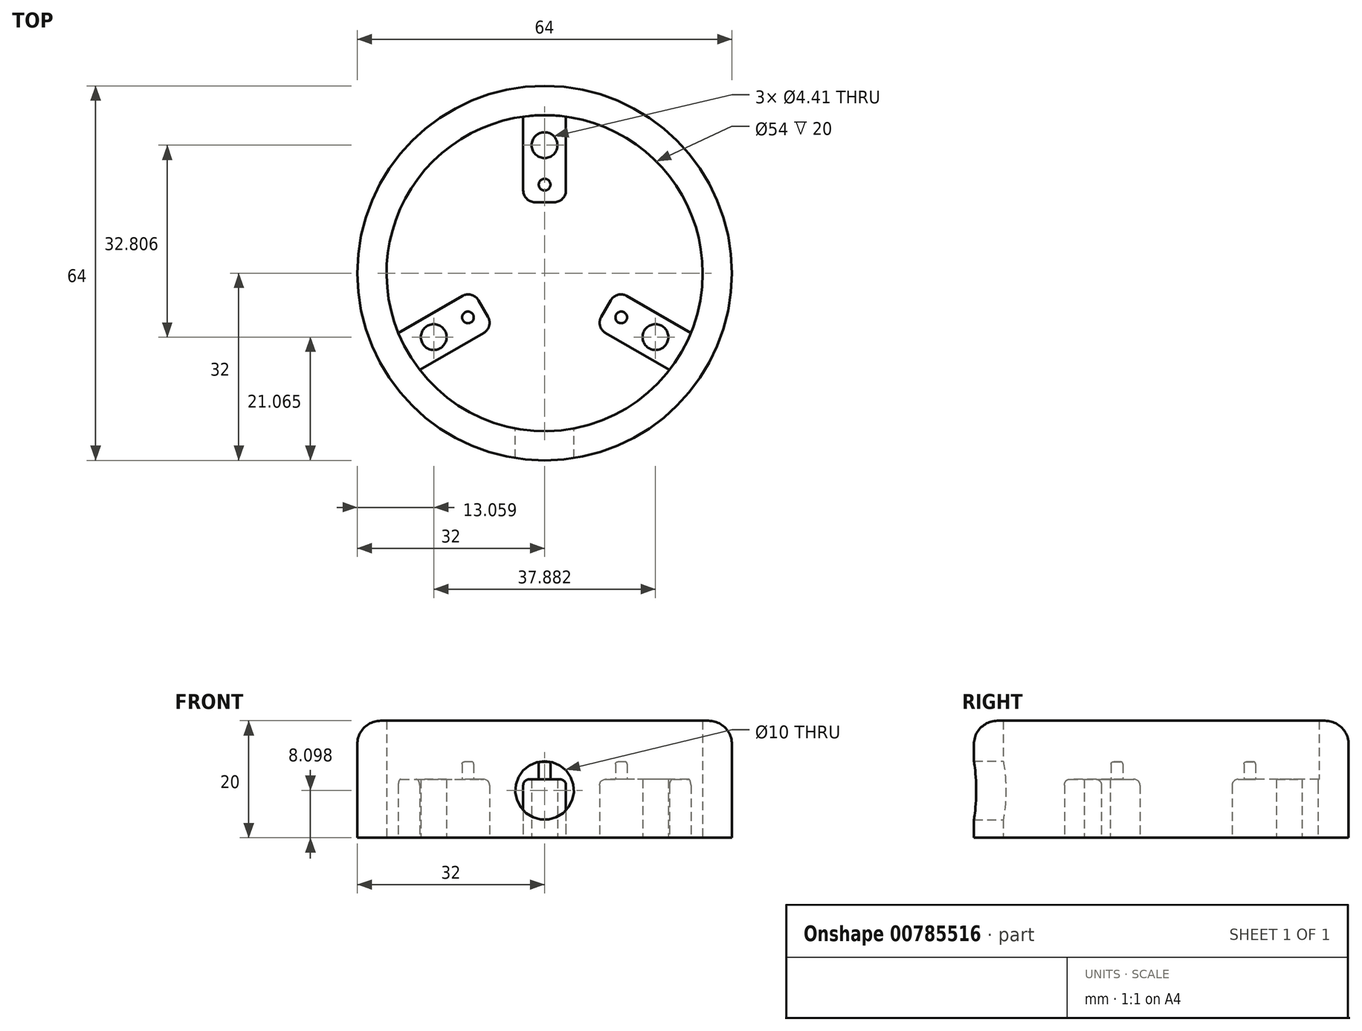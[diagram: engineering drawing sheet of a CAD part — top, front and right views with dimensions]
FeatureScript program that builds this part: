
annotation { "Feature Type Name" : "Feature", "Feature Type Description" : "" }
export const myFeature = defineFeature(function(context is Context, id is Id, definition is map)
    precondition{}
    {
        {
            var Q0;
            Q0=qCreatedBy(makeId("Top.planeOp"),FACE);
            var sketch = newSketch(context, id + "F0", { "sketchPlane" : qUnion([Q0])});
            skCircle(sketch, "E0", {"center": v(0, 0) * mm, "radius": 27 * mm});
            skCircle(sketch, "E1", {"center": v(0, 15.13) * mm, "radius": 1 * mm});
            skCircle(sketch, "E2.1.0", {"center": v(-13.1, -7.56) * mm, "radius": 1 * mm});
            skCircle(sketch, "E2.2.0", {"center": v(13.1, -7.56) * mm, "radius": 1 * mm});
            skLineSegment(sketch, "E3.right", {"start": v(3.65, 26.75) * mm, "end": v(3.65, 14.13) * mm});
            skLineSegment(sketch, "E4.1.0", {"start": v(-21.34, -16.54) * mm, "end": v(-10.4, -10.23) * mm});
            skLineSegment(sketch, "E4.1.1", {"start": v(-25, -10.21) * mm, "end": v(-14.06, -3.9) * mm});
            skLineSegment(sketch, "E4.2.0", {"start": v(25, -10.21) * mm, "end": v(14.06, -3.9) * mm});
            skLineSegment(sketch, "E4.2.1", {"start": v(21.34, -16.54) * mm, "end": v(10.4, -10.23) * mm});
            skPoint(sketch, "E5.orphan", {"position": v(-3.65, 29.24) * mm});
            skPoint(sketch, "E6.orphan", {"position": v(3.65, 29.24) * mm});
            skPoint(sketch, "E7.orphan", {"position": v(27.15, -11.46) * mm});
            skPoint(sketch, "E8.orphan", {"position": v(23.5, -17.78) * mm});
            skPoint(sketch, "E9.orphan", {"position": v(-27.15, -11.46) * mm});
            skPoint(sketch, "E10.orphan", {"position": v(-23.5, -17.78) * mm});
            skLineSegment(sketch, "E11", {"start": v(-1.65, 12.13) * mm, "end": v(1.65, 12.13) * mm});
            skLineSegment(sketch, "E12", {"start": v(-9.68, -7.5) * mm, "end": v(-11.33, -4.63) * mm});
            skLineSegment(sketch, "E13", {"start": v(9.68, -7.5) * mm, "end": v(11.33, -4.63) * mm});
            skPoint(sketch, "E14.trimOffspring.end.orphan", {"position": v(3.65, 1.01) * mm});
            skPoint(sketch, "E15.trimOffspring.end.orphan", {"position": v(-3.65, 1.01) * mm});
            skLineSegment(sketch, "E16", {"start": v(-3.65, 14.13) * mm, "end": v(-3.65, 26.75) * mm});
            skCircle(sketch, "E17.0", {"center": v(0, 0) * mm, "radius": 32 * mm});
            skCircle(sketch, "E18", {"center": v(0, 21.87) * mm, "radius": 2.2 * mm});
            skCircle(sketch, "E19.1.0", {"center": v(-18.94, -10.94) * mm, "radius": 2.2 * mm});
            skCircle(sketch, "E19.2.0", {"center": v(18.94, -10.94) * mm, "radius": 2.2 * mm});
            skPoint(sketch, "E20.visualSharp", {"position": v(-3.65, 12.13) * mm});
            skArc(sketch, "E20.filletArc", {"start": v(-3.65, 14.13) * mm, "mid": v(-3.07, 12.71) * mm, "end": v(-1.65, 12.13) * mm});
            skPoint(sketch, "E21.visualSharp", {"position": v(3.65, 12.13) * mm});
            skArc(sketch, "E21.filletArc", {"start": v(1.65, 12.13) * mm, "mid": v(3.07, 12.71) * mm, "end": v(3.65, 14.13) * mm});
            skPoint(sketch, "E22.visualSharp", {"position": v(12.33, -2.9) * mm});
            skArc(sketch, "E22.filletArc", {"start": v(14.06, -3.9) * mm, "mid": v(12.54, -3.7) * mm, "end": v(11.33, -4.63) * mm});
            skPoint(sketch, "E23.visualSharp", {"position": v(8.68, -9.23) * mm});
            skArc(sketch, "E23.filletArc", {"start": v(9.68, -7.5) * mm, "mid": v(9.48, -9.01) * mm, "end": v(10.4, -10.23) * mm});
            skPoint(sketch, "E24.visualSharp", {"position": v(-8.68, -9.23) * mm});
            skArc(sketch, "E24.filletArc", {"start": v(-10.4, -10.23) * mm, "mid": v(-9.48, -9.01) * mm, "end": v(-9.68, -7.5) * mm});
            skPoint(sketch, "E25.visualSharp", {"position": v(-12.33, -2.9) * mm});
            skArc(sketch, "E25.filletArc", {"start": v(-11.33, -4.63) * mm, "mid": v(-12.54, -3.7) * mm, "end": v(-14.06, -3.9) * mm});
            skSolve(sketch);
        }
        {
            var Q0;
            Q0=makeQuery(id+"F0.imprint","IMPRINT",FACE,{"disambiguationData":[TD([[makeQuery(id+"F0.imprint","IMPRINT",EDGE,{"derivedFrom":sQuery(id+"F0.wireOp",EDGE,"E17.0")}),1.0]])]});
            extrude(context, id + "F1", {"entities" : qUnion([Q0]), "depth" : 20 * mm, "offsetDistance" : 25 * mm});
        }
        {
            var Q0;
            Q0=makeQuery(id+"F0.imprint","IMPRINT",FACE,{"disambiguationData":[TD([[makeQuery(id+"F0.imprint","IMPRINT",EDGE,{"derivedFrom":sQuery(id+"F0.wireOp",EDGE,"E1")}),-1.0]])]});
            var Q1;
            Q1=makeQuery(id+"F0.imprint","IMPRINT",FACE,{"disambiguationData":[TD([[makeQuery(id+"F0.imprint","IMPRINT",EDGE,{"derivedFrom":sQuery(id+"F0.wireOp",EDGE,"E2.1.0")}),-1.0]])]});
            var Q2;
            Q2=makeQuery(id+"F0.imprint","IMPRINT",FACE,{"disambiguationData":[TD([[makeQuery(id+"F0.imprint","IMPRINT",EDGE,{"derivedFrom":sQuery(id+"F0.wireOp",EDGE,"E2.2.0")}),-1.0]])]});
            extrude(context, id + "F2", {"entities" : qUnion([Q0, Q1, Q2]), "operationType" : NewBodyOperationType.ADD, "depth" : 10 * mm, "offsetDistance" : 25 * mm});
        }
        {
            var Q0;
            Q0=makeQuery(id+"F1.opExtrude","CAP_EDGE",EDGE,{"disambiguationData":[OSD([sQuery(id+"F0.wireOp",EDGE,"E17.0")])],"isStart":false});
            fillet(context, id + "F3", {"entities" : qUnion([Q0]), "radius" : 4 * mm, "tangentPropagation" : true, "allowEdgeOverflow" : false});
        }
        {
            var Q0;
            Q0=makeQuery(id+"F2.opExtrude","CAP_EDGE",EDGE,{"disambiguationData":[OSD([sQuery(id+"F0.wireOp",EDGE,"E16")])],"isStart":false});
            var Q1;
            Q1=makeQuery(id+"F2.opExtrude","CAP_EDGE",EDGE,{"disambiguationData":[OSD([sQuery(id+"F0.wireOp",EDGE,"E20.filletArc")])],"isStart":false});
            var Q2;
            Q2=makeQuery(id+"F2.opExtrude","CAP_EDGE",EDGE,{"disambiguationData":[OSD([sQuery(id+"F0.wireOp",EDGE,"E11")])],"isStart":false});
            var Q3;
            Q3=makeQuery(id+"F2.opExtrude","CAP_EDGE",EDGE,{"disambiguationData":[OSD([sQuery(id+"F0.wireOp",EDGE,"E21.filletArc")])],"isStart":false});
            var Q4;
            Q4=makeQuery(id+"F2.opExtrude","CAP_EDGE",EDGE,{"disambiguationData":[OSD([sQuery(id+"F0.wireOp",EDGE,"E3.right")])],"isStart":false});
            var Q5;
            Q5=makeQuery(id+"F2.opExtrude","CAP_EDGE",EDGE,{"disambiguationData":[OSD([sQuery(id+"F0.wireOp",EDGE,"E13")])],"isStart":false});
            var Q6;
            Q6=makeQuery(id+"F2.opExtrude","CAP_EDGE",EDGE,{"disambiguationData":[OSD([sQuery(id+"F0.wireOp",EDGE,"E12")])],"isStart":false});
            fillet(context, id + "F4", {"entities" : qUnion([Q0, Q1, Q2, Q3, Q4, Q5, Q6]), "radius" : 1 * mm, "tangentPropagation" : true, "allowEdgeOverflow" : false});
        }
        {
            var Q0;
            Q0=makeQuery(id+"F0.imprint","IMPRINT",FACE,{"disambiguationData":[TD([[makeQuery(id+"F0.imprint","IMPRINT",EDGE,{"derivedFrom":sQuery(id+"F0.wireOp",EDGE,"E1")}),1.0]])]});
            var Q1;
            Q1=makeQuery(id+"F0.imprint","IMPRINT",FACE,{"disambiguationData":[TD([[makeQuery(id+"F0.imprint","IMPRINT",EDGE,{"derivedFrom":sQuery(id+"F0.wireOp",EDGE,"E2.2.0")}),1.0]])]});
            var Q2;
            Q2=makeQuery(id+"F0.imprint","IMPRINT",FACE,{"disambiguationData":[TD([[makeQuery(id+"F0.imprint","IMPRINT",EDGE,{"derivedFrom":sQuery(id+"F0.wireOp",EDGE,"E2.1.0")}),1.0]])]});
            extrude(context, id + "F5", {"entities" : qUnion([Q0, Q1, Q2]), "operationType" : NewBodyOperationType.ADD, "depth" : 13 * mm, "offsetDistance" : 25 * mm});
        }
        {
            var Q0;
            Q0=makeQuery(id+"F5.opExtrude","CAP_EDGE",EDGE,{"disambiguationData":[OSD([sQuery(id+"F0.wireOp",EDGE,"E2.1.0")])],"isStart":false});
            var Q1;
            Q1=makeQuery(id+"F5.opExtrude","CAP_EDGE",EDGE,{"disambiguationData":[OSD([sQuery(id+"F0.wireOp",EDGE,"E2.2.0")])],"isStart":false});
            var Q2;
            Q2=makeQuery(id+"F5.opExtrude","CAP_EDGE",EDGE,{"disambiguationData":[OSD([sQuery(id+"F0.wireOp",EDGE,"E1")])],"isStart":false});
            var Q3;
            Q3=makeQuery(id+"F2.opExtrude","CAP_EDGE",EDGE,{"disambiguationData":[OSD([sQuery(id+"F0.wireOp",EDGE,"E2.1.0")])],"isStart":false});
            var Q4;
            Q4=makeQuery(id+"F2.opExtrude","CAP_EDGE",EDGE,{"disambiguationData":[OSD([sQuery(id+"F0.wireOp",EDGE,"E2.2.0")])],"isStart":false});
            var Q5;
            Q5=makeQuery(id+"F2.opExtrude","CAP_EDGE",EDGE,{"disambiguationData":[OSD([sQuery(id+"F0.wireOp",EDGE,"E1")])],"isStart":false});
            fillet(context, id + "F6", {"entities" : qUnion([Q0, Q1, Q2, Q3, Q4, Q5]), "radius" : .4 * mm, "tangentPropagation" : true, "allowEdgeOverflow" : false});
        }
        {
            var Q0;
            Q0=qCreatedBy(makeId("Front.planeOp"),FACE);
            var sketch = newSketch(context, id + "F7", { "sketchPlane" : qUnion([Q0])});
            skCircle(sketch, "E26", {"center": v(0, 8.1) * mm, "radius": 5 * mm});
            skSolve(sketch);
        }
        {
            var Q0;
            Q0 = qSketchRegion(id + "F7", true);
            extrude(context, id + "F8", {"entities" : qUnion([Q0]), "operationType" : NewBodyOperationType.REMOVE, "depth" : 50 * mm, "offsetDistance" : 25 * mm});
        }
    });
